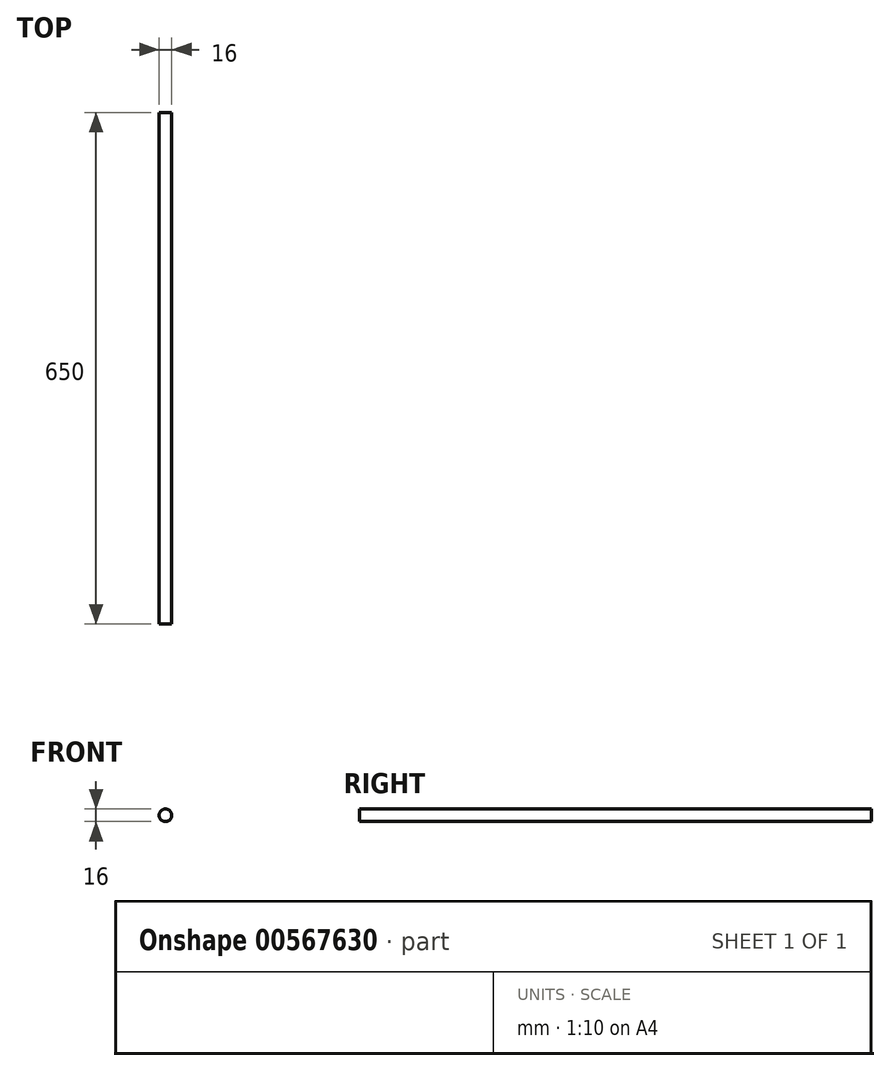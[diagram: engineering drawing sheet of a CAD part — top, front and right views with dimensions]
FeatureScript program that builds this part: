
annotation { "Feature Type Name" : "Feature", "Feature Type Description" : "" }
export const myFeature = defineFeature(function(context is Context, id is Id, definition is map)
    precondition{}
    {
        {
            var Q0;
            Q0=qCreatedBy(makeId("Front.planeOp"),FACE);
            var sketch = newSketch(context, id + "F0", { "sketchPlane" : qUnion([Q0])});
            skCircle(sketch, "E0", {"center": v(0, 0) * mm, "radius": 8 * mm});
            skSolve(sketch);
        }
        {
            var Q0;
            Q0 = qSketchRegion(id + "F0", true);
            extrude(context, id + "F1", {"entities" : qUnion([Q0]), "oppositeDirection" : true, "depth" : 650 * mm, "offsetDistance" : 25.4 * mm});
        }
    });
